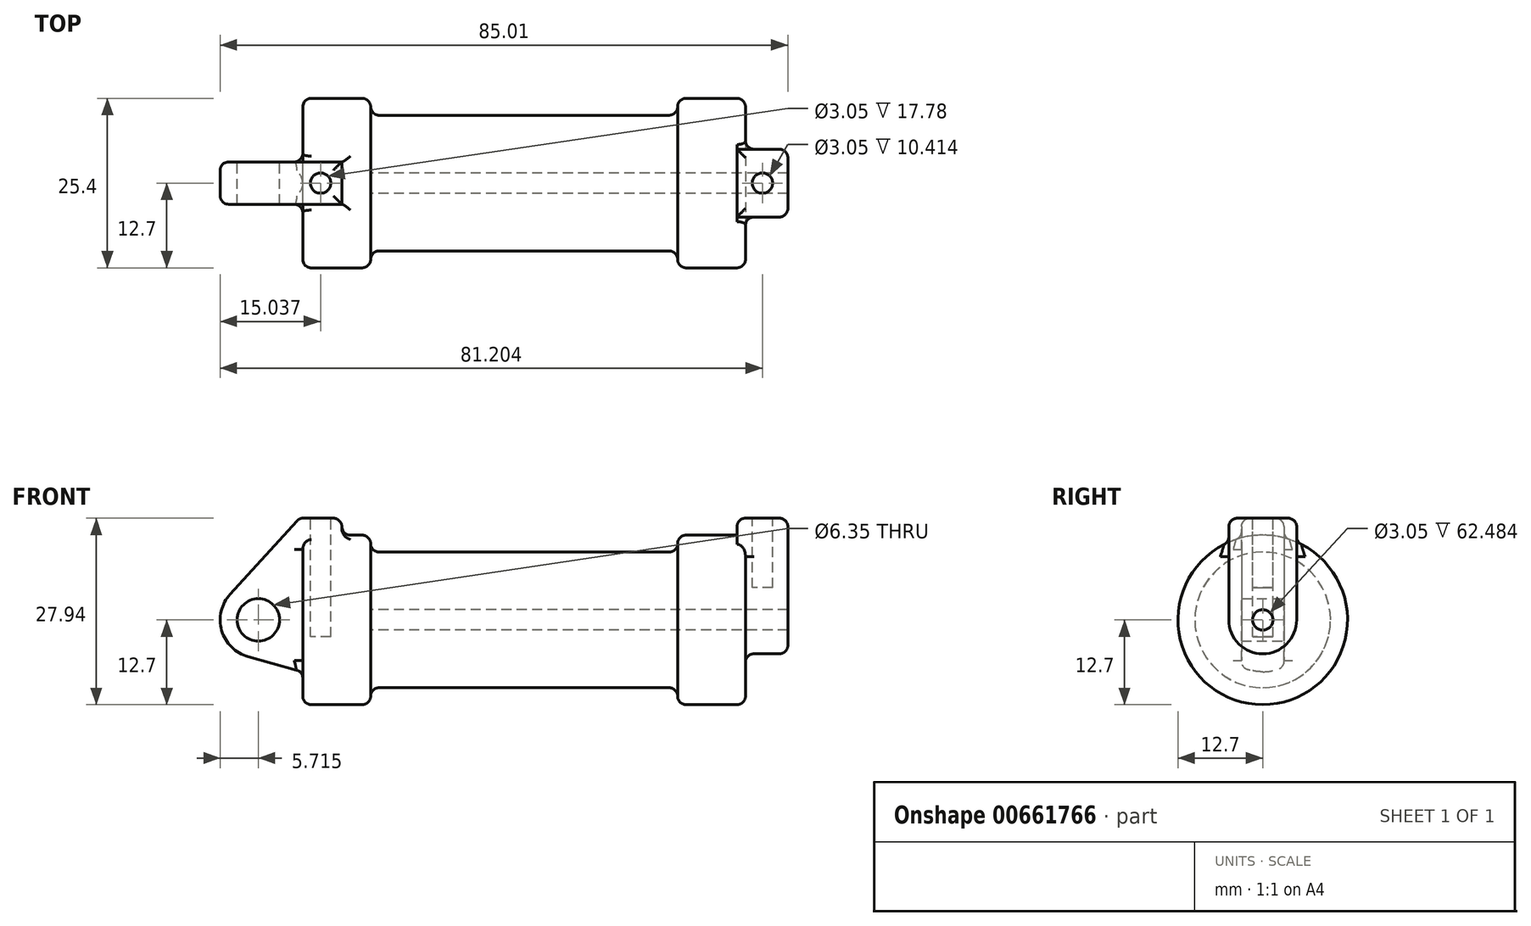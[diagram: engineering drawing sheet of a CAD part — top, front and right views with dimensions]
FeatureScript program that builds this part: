
annotation { "Feature Type Name" : "Feature", "Feature Type Description" : "" }
export const myFeature = defineFeature(function(context is Context, id is Id, definition is map)
    precondition{}
    {
        {
            var Q0;
            Q0=qCreatedBy(makeId("Front.planeOp"),FACE);
            var sketch = newSketch(context, id + "F0", { "sketchPlane" : qUnion([Q0])});
            skLineSegment(sketch, "E0", {"start": v(0, 0) * mm, "end": v(0, 12.7) * mm});
            skLineSegment(sketch, "E1", {"start": v(0, 12.7) * mm, "end": v(10.16, 12.7) * mm});
            skLineSegment(sketch, "E2", {"start": v(10.16, 12.7) * mm, "end": v(10.16, 10.16) * mm});
            skLineSegment(sketch, "E3", {"start": v(10.16, 10.16) * mm, "end": v(56.13, 10.16) * mm});
            skLineSegment(sketch, "E4", {"start": v(56.13, 10.16) * mm, "end": v(56.13, 12.7) * mm});
            skLineSegment(sketch, "E5", {"start": v(56.13, 12.7) * mm, "end": v(66.3, 12.7) * mm});
            skLineSegment(sketch, "E6", {"start": v(66.3, 12.7) * mm, "end": v(66.3, 0) * mm});
            skLineSegment(sketch, "E7", {"start": v(66.3, 0) * mm, "end": v(0, 0) * mm});
            skLineSegment(sketch, "E8", {"start": v(5.84, 15.24) * mm, "end": v(-0.5, 15.24) * mm});
            skLineSegment(sketch, "E9", {"start": v(-0.5, 15.24) * mm, "end": v(-10.88, 3.85) * mm});
            skLineSegment(sketch, "E10", {"start": v(0, 0) * mm, "end": v(-6.65, 0) * mm});
            skCircle(sketch, "E11", {"center": v(-6.65, 0) * mm, "radius": 5.72 * mm});
            skCircle(sketch, "E12", {"center": v(-6.65, 0) * mm, "radius": 3.18 * mm});
            skLineSegment(sketch, "E13", {"start": v(5.84, 15.24) * mm, "end": v(5.84, -9.4) * mm});
            skLineSegment(sketch, "E14", {"start": v(5.84, -9.4) * mm, "end": v(-8.18, -5.5) * mm});
            skSolve(sketch);
        }
        {
            var Q0;
            {var subQ0=sQuery(id+"F0.wireOp",EDGE,"E2");Q0=makeQuery(id+"F0.imprint","IMPRINT",FACE,{"disambiguationData":[TD([[makeQuery(id+"F0.imprint","IMPRINT",EDGE,{"derivedFrom":subQ0}),-1.0]])]});}
            var Q1;
            {var subQ0=sQuery(id+"F0.wireOp",EDGE,"E0");Q1=makeQuery(id+"F0.imprint","IMPRINT",FACE,{"disambiguationData":[TD([[makeQuery(id+"F0.imprint","IMPRINT",EDGE,{"derivedFrom":subQ0}),-1.0]])]});}
            var Q2;
            Q2=sQuery(id+"F0.wireOp",EDGE,"E7");
            revolve(context, id + "F1", {"entities" : qUnion([Q0, Q1]), "axis" : qUnion([Q2]), "revolveType" : RevolveType.FULL});
        }
        {
            var Q0;
            {var subQ0=sQuery(id+"F0.wireOp",EDGE,"E0");Q0=makeQuery(id+"F0.imprint","IMPRINT",FACE,{"disambiguationData":[TD([[makeQuery(id+"F0.imprint","IMPRINT",EDGE,{"derivedFrom":subQ0}),-1.0]])]});}
            var Q1;
            {var subQ1=sQuery(id+"F0.wireOp",EDGE,"E0");Q1=makeQuery(id+"F0.imprint","IMPRINT",FACE,{"disambiguationData":[TD([[makeQuery(id+"F0.imprint","IMPRINT",EDGE,{"derivedFrom":subQ1}),1.0]])]});}
            var Q2;
            {var subQ0=sQuery(id+"F0.wireOp",EDGE,"E14");Q2=makeQuery(id+"F0.imprint","IMPRINT",FACE,{"disambiguationData":[TD([[makeQuery(id+"F0.imprint","IMPRINT",EDGE,{"derivedFrom":subQ0}),-1.0]])]});}
            var Q3;
            {var subQ5=sQuery(id+"F0.wireOp",EDGE,"E12");Q3=makeQuery(id+"F0.imprint","IMPRINT",FACE,{"disambiguationData":[TD([[makeQuery(id+"F0.imprint","IMPRINT",EDGE,{"derivedFrom":subQ5}),-1.0]])]});}
            extrude(context, id + "F2", {"entities" : qUnion([Q0, Q1, Q2, Q3]), "operationType" : NewBodyOperationType.ADD, "endBound" : BoundingType.SYMMETRIC, "depth" : 6.35 * mm});
        }
        {
            var Q0;
            Q0=makeQuery(id+"F1.opRevolve","SWEPT_FACE",FACE,{"disambiguationData":[OSD([sQuery(id+"F0.wireOp",EDGE,"E6")])]});
            var sketch = newSketch(context, id + "F3", { "sketchPlane" : qUnion([Q0])});
            skCircle(sketch, "E15", {"center": v(0, 0) * mm, "radius": 1.52 * mm});
            skCircle(sketch, "E16", {"center": v(0, 0) * mm, "radius": 5.08 * mm});
            skLineSegment(sketch, "E17", {"start": v(5.08, 0) * mm, "end": v(5.08, 15.24) * mm});
            skLineSegment(sketch, "E18", {"start": v(-5.08, 0) * mm, "end": v(-5.08, 15.24) * mm});
            skLineSegment(sketch, "E19", {"start": v(-5.08, 15.24) * mm, "end": v(5.08, 15.24) * mm});
            skSolve(sketch);
        }
        {
            var Q0;
            Q0=makeQuery(id+"F2.opExtrude","SWEPT_FACE",FACE,{"disambiguationData":[OSD([sQuery(id+"F0.wireOp",EDGE,"E8")])]});
            var sketch = newSketch(context, id + "F4", { "sketchPlane" : qUnion([Q0])});
            skCircle(sketch, "E20", {"center": v(2.67, 0) * mm, "radius": 1.52 * mm});
            skSolve(sketch);
        }
        {
            var Q0;
            Q0=qSketchRegion(id+"F4",true);
            extrude(context, id + "F5", {"entities" : qUnion([Q0]), "operationType" : NewBodyOperationType.REMOVE, "oppositeDirection" : true, "depth" : 17.78 * mm});
        }
        {
            var Q0;
            {var subQ0=sQuery(id+"F3.wireOp",EDGE,"E19");Q0=makeQuery(id+"F3.imprint","IMPRINT",FACE,{"disambiguationData":[TD([[makeQuery(id+"F3.imprint","IMPRINT",EDGE,{"derivedFrom":subQ0}),-1.0]])]});}
            extrude(context, id + "F6", {"entities" : qUnion([Q0]), "operationType" : NewBodyOperationType.ADD, "oppositeDirection" : true, "depth" : 1.27 * mm});
        }
        {
            var Q0;
            {var subQ0=sQuery(id+"F3.wireOp",EDGE,"E17");var subQ1=sQuery(id+"F3.wireOp",EDGE,"E16");var subQ2=makeQuery(id+"F3.imprint","INTERSECT",VERTEX,{"derivedFrom":[subQ1,subQ0]});Q0=makeQuery(id+"F3.imprint","IMPRINT",FACE,{"disambiguationData":[TD([[makeQuery(id+"F3.imprint","IMPRINT",EDGE,{"disambiguationData":[TD([[subQ2,-1.0]])],"derivedFrom":subQ1}),-1.0]])]});}
            var Q1;
            Q1=makeQuery(id+"F3.imprint","IMPRINT",FACE,{"disambiguationData":[TD([[makeQuery(id+"F3.imprint","IMPRINT",EDGE,{"derivedFrom":sQuery(id+"F3.wireOp",EDGE,"E15")}),-1.0]])]});
            var Q2;
            {var subQ0=sQuery(id+"F3.wireOp",EDGE,"E19");Q2=makeQuery(id+"F3.imprint","IMPRINT",FACE,{"disambiguationData":[TD([[makeQuery(id+"F3.imprint","IMPRINT",EDGE,{"derivedFrom":subQ0}),-1.0]])]});}
            extrude(context, id + "F7", {"entities" : qUnion([Q0, Q1, Q2]), "operationType" : NewBodyOperationType.ADD, "depth" : 6.35 * mm});
        }
        {
            var Q0;
            Q0=makeQuery(id+"F3.imprint","IMPRINT",FACE,{"disambiguationData":[TD([[makeQuery(id+"F3.imprint","IMPRINT",EDGE,{"derivedFrom":sQuery(id+"F3.wireOp",EDGE,"E15")}),1.0]])]});
            var Q1;
            Q1=makeQuery(id+"F1.opRevolve","SWEPT_FACE",FACE,{"disambiguationData":[OSD([sQuery(id+"F0.wireOp",EDGE,"E2")])]});
            extrude(context, id + "F8", {"entities" : qUnion([Q0]), "operationType" : NewBodyOperationType.REMOVE, "endBound" : BoundingType.UP_TO_SURFACE, "oppositeDirection" : true, "endBoundEntityFace" : qUnion([Q1]), "depth" : 25.4 * mm});
        }
        {
            var Q0;
            {var subQ0=sQuery(id+"F3.wireOp",EDGE,"E19");Q0=makeQuery(id+"F7.boolean.opBoolean","MERGE",FACE,{"derivedFrom":[makeQuery(id+"F6.opExtrude","SWEPT_FACE",FACE,{"disambiguationData":[OSD([subQ0])]}),makeQuery(id+"F7.opExtrude","SWEPT_FACE",FACE,{"disambiguationData":[OSD([subQ0])]})]});}
            var sketch = newSketch(context, id + "F9", { "sketchPlane" : qUnion([Q0])});
            skLineSegment(sketch, "E21", {"start": v(68.83, 5.08) * mm, "end": v(68.83, -5.08) * mm, "construction": true});
            skLineSegment(sketch, "E22", {"start": v(72.64, 0) * mm, "end": v(65.02, 0) * mm, "construction": true});
            skCircle(sketch, "E23", {"center": v(68.83, 0) * mm, "radius": 1.52 * mm});
            skSolve(sketch);
        }
        {
            var Q0;
            Q0=makeQuery(id+"F9.imprint","IMPRINT",FACE,{"disambiguationData":[TD([[makeQuery(id+"F9.imprint","IMPRINT",EDGE,{"derivedFrom":sQuery(id+"F9.wireOp",EDGE,"E23")}),1.0]])]});
            extrude(context, id + "F10", {"entities" : qUnion([Q0]), "operationType" : NewBodyOperationType.REMOVE, "oppositeDirection" : true, "depth" : 10.4 * mm});
        }
        {
            var Q0;
            Q0=makeQuery(id+"F1.opRevolve","SWEPT_EDGE",EDGE,{"disambiguationData":[OSD([sQuery(id+"F0.wireOp",EDGE,"E1"),sQuery(id+"F0.wireOp",EDGE,"E2")])]});
            var Q1;
            Q1=makeQuery(id+"F1.opRevolve","SWEPT_EDGE",EDGE,{"disambiguationData":[OSD([sQuery(id+"F0.wireOp",EDGE,"E4"),sQuery(id+"F0.wireOp",EDGE,"E5")])]});
            var Q2;
            Q2=makeQuery(id+"F1.opRevolve","SWEPT_EDGE",EDGE,{"disambiguationData":[OSD([sQuery(id+"F0.wireOp",EDGE,"E0"),sQuery(id+"F0.wireOp",EDGE,"E1")])]});
            var Q3;
            Q3=makeQuery(id+"F1.opRevolve","SWEPT_EDGE",EDGE,{"disambiguationData":[OSD([sQuery(id+"F0.wireOp",EDGE,"E5"),sQuery(id+"F0.wireOp",EDGE,"E6")])]});
            var Q4;
            Q4=makeQuery(id+"F1.opRevolve","SWEPT_EDGE",EDGE,{"disambiguationData":[OSD([sQuery(id+"F0.wireOp",EDGE,"E2"),sQuery(id+"F0.wireOp",EDGE,"E3")])]});
            var Q5;
            Q5=makeQuery(id+"F1.opRevolve","SWEPT_EDGE",EDGE,{"disambiguationData":[OSD([sQuery(id+"F0.wireOp",EDGE,"E3"),sQuery(id+"F0.wireOp",EDGE,"E4")])]});
            fillet(context, id + "F11", {"entities" : qUnion([Q0, Q1, Q2, Q3, Q4, Q5]), "radius" : 1.27 * mm, "tangentPropagation" : true, "allowEdgeOverflow" : false});
        }
        {
            var Q0;
            Q0=makeQuery(id+"F2.opExtrude","CAP_EDGE",EDGE,{"disambiguationData":[OSD([sQuery(id+"F0.wireOp",EDGE,"E8")])],"isStart":true});
            var Q1;
            Q1=makeQuery(id+"F2.opExtrude","SWEPT_EDGE",EDGE,{"disambiguationData":[OSD([sQuery(id+"F0.wireOp",EDGE,"E8"),sQuery(id+"F0.wireOp",EDGE,"E9")])]});
            var Q2;
            Q2=makeQuery(id+"F2.opExtrude","SWEPT_EDGE",EDGE,{"disambiguationData":[OSD([sQuery(id+"F0.wireOp",EDGE,"E8"),sQuery(id+"F0.wireOp",EDGE,"E13")])]});
            var Q3;
            Q3=makeQuery(id+"F2.opExtrude","CAP_EDGE",EDGE,{"disambiguationData":[OSD([sQuery(id+"F0.wireOp",EDGE,"E8")])],"isStart":false});
            var Q4;
            Q4=makeQuery(id+"F2.boolean.opBoolean","INTERSECT",EDGE,{"derivedFrom":[makeQuery(id+"F1.opRevolve","SWEPT_FACE",FACE,{"disambiguationData":[OSD([sQuery(id+"F0.wireOp",EDGE,"E1")])]}),makeQuery(id+"F2.opExtrude","SWEPT_FACE",FACE,{"disambiguationData":[OSD([sQuery(id+"F0.wireOp",EDGE,"E13")])]})]});
            var Q5;
            Q5=makeQuery(id+"F2.boolean.opBoolean","INTERSECT",EDGE,{"derivedFrom":[makeQuery(id+"F1.opRevolve","SWEPT_FACE",FACE,{"disambiguationData":[OSD([sQuery(id+"F0.wireOp",EDGE,"E1")])]}),makeQuery(id+"F2.opExtrude","CAP_FACE",FACE,{"disambiguationData":[OSD([sQuery(id+"F0.wireOp",EDGE,"E8"),sQuery(id+"F0.wireOp",EDGE,"E9"),sQuery(id+"F0.wireOp",EDGE,"E11"),sQuery(id+"F0.wireOp",EDGE,"E12"),sQuery(id+"F0.wireOp",EDGE,"E13"),sQuery(id+"F0.wireOp",EDGE,"E14")])],"isStart":false})]});
            var Q6;
            {var subQ0=sQuery(id+"F0.wireOp",EDGE,"E1");Q6=makeQuery(id+"F11.opFillet","BLEND_EDGE",EDGE,{"blendedFrom":[makeQuery(id+"F1.opRevolve","SWEPT_EDGE",EDGE,{"disambiguationData":[OSD([sQuery(id+"F0.wireOp",EDGE,"E0"),subQ0])]}),makeQuery(id+"F1.opRevolve","SWEPT_FACE",FACE,{"disambiguationData":[OSD([subQ0])]})],"blendedInto":[makeQuery(id+"F1.opRevolve","SWEPT_FACE",FACE,{"disambiguationData":[OSD([subQ0])]})]});}
            var Q7;
            Q7=makeQuery(id+"F2.boolean.opBoolean","INTERSECT",EDGE,{"derivedFrom":[makeQuery(id+"F1.opRevolve","SWEPT_FACE",FACE,{"disambiguationData":[OSD([sQuery(id+"F0.wireOp",EDGE,"E1")])]}),makeQuery(id+"F2.opExtrude","CAP_FACE",FACE,{"disambiguationData":[OSD([sQuery(id+"F0.wireOp",EDGE,"E8"),sQuery(id+"F0.wireOp",EDGE,"E9"),sQuery(id+"F0.wireOp",EDGE,"E11"),sQuery(id+"F0.wireOp",EDGE,"E12"),sQuery(id+"F0.wireOp",EDGE,"E13"),sQuery(id+"F0.wireOp",EDGE,"E14")])],"isStart":true})]});
            var Q8;
            Q8=makeQuery(id+"F2.opExtrude","CAP_EDGE",EDGE,{"disambiguationData":[OSD([sQuery(id+"F0.wireOp",EDGE,"E9")])],"isStart":true});
            var Q9;
            Q9=makeQuery(id+"F2.opExtrude","CAP_EDGE",EDGE,{"disambiguationData":[OSD([sQuery(id+"F0.wireOp",EDGE,"E9")])],"isStart":false});
            var Q10;
            Q10=makeQuery(id+"F7.opExtrude","CAP_EDGE",EDGE,{"disambiguationData":[OSD([sQuery(id+"F3.wireOp",EDGE,"E17")])],"isStart":false});
            var Q11;
            Q11=makeQuery(id+"F7.opExtrude","CAP_EDGE",EDGE,{"disambiguationData":[OSD([sQuery(id+"F3.wireOp",EDGE,"E18")])],"isStart":false});
            var Q12;
            Q12=makeQuery(id+"F7.opExtrude","CAP_EDGE",EDGE,{"disambiguationData":[OSD([sQuery(id+"F3.wireOp",EDGE,"E19")])],"isStart":false});
            var Q13;
            {var subQ0=sQuery(id+"F3.wireOp",EDGE,"E19");var subQ1=sQuery(id+"F3.wireOp",EDGE,"E18");Q13=makeQuery(id+"F7.boolean.opBoolean","MERGE",EDGE,{"derivedFrom":[makeQuery(id+"F6.opExtrude","SWEPT_EDGE",EDGE,{"disambiguationData":[OSD([subQ1,subQ0])]}),makeQuery(id+"F7.opExtrude","SWEPT_EDGE",EDGE,{"disambiguationData":[OSD([subQ1,subQ0])]})]});}
            var Q14;
            {var subQ0=sQuery(id+"F3.wireOp",EDGE,"E19");var subQ1=sQuery(id+"F3.wireOp",EDGE,"E17");Q14=makeQuery(id+"F7.boolean.opBoolean","MERGE",EDGE,{"derivedFrom":[makeQuery(id+"F6.opExtrude","SWEPT_EDGE",EDGE,{"disambiguationData":[OSD([subQ1,subQ0])]}),makeQuery(id+"F7.opExtrude","SWEPT_EDGE",EDGE,{"disambiguationData":[OSD([subQ1,subQ0])]})]});}
            var Q15;
            Q15=makeQuery(id+"F6.opExtrude","CAP_EDGE",EDGE,{"disambiguationData":[OSD([sQuery(id+"F0.wireOp",EDGE,"E5"),sQuery(id+"F0.wireOp",EDGE,"E6")])],"isStart":false});
            var Q16;
            Q16=makeQuery(id+"F6.opExtrude","CAP_EDGE",EDGE,{"disambiguationData":[OSD([sQuery(id+"F3.wireOp",EDGE,"E19")])],"isStart":false});
            var Q17;
            Q17=makeQuery(id+"F7.opExtrude","CAP_EDGE",EDGE,{"disambiguationData":[OSD([sQuery(id+"F3.wireOp",EDGE,"E18")])],"isStart":true});
            var Q18;
            Q18=makeQuery(id+"F7.opExtrude","CAP_EDGE",EDGE,{"disambiguationData":[OSD([sQuery(id+"F3.wireOp",EDGE,"E16")])],"isStart":true});
            var Q19;
            Q19=makeQuery(id+"F7.opExtrude","CAP_EDGE",EDGE,{"disambiguationData":[OSD([sQuery(id+"F3.wireOp",EDGE,"E17")])],"isStart":true});
            fillet(context, id + "F12", {"entities" : qUnion([Q0, Q1, Q2, Q3, Q4, Q5, Q6, Q7, Q8, Q9, Q10, Q11, Q12, Q13, Q14, Q15, Q16, Q17, Q18, Q19]), "radius" : 1.27 * mm, "tangentPropagation" : true, "allowEdgeOverflow" : false});
        }
    });
